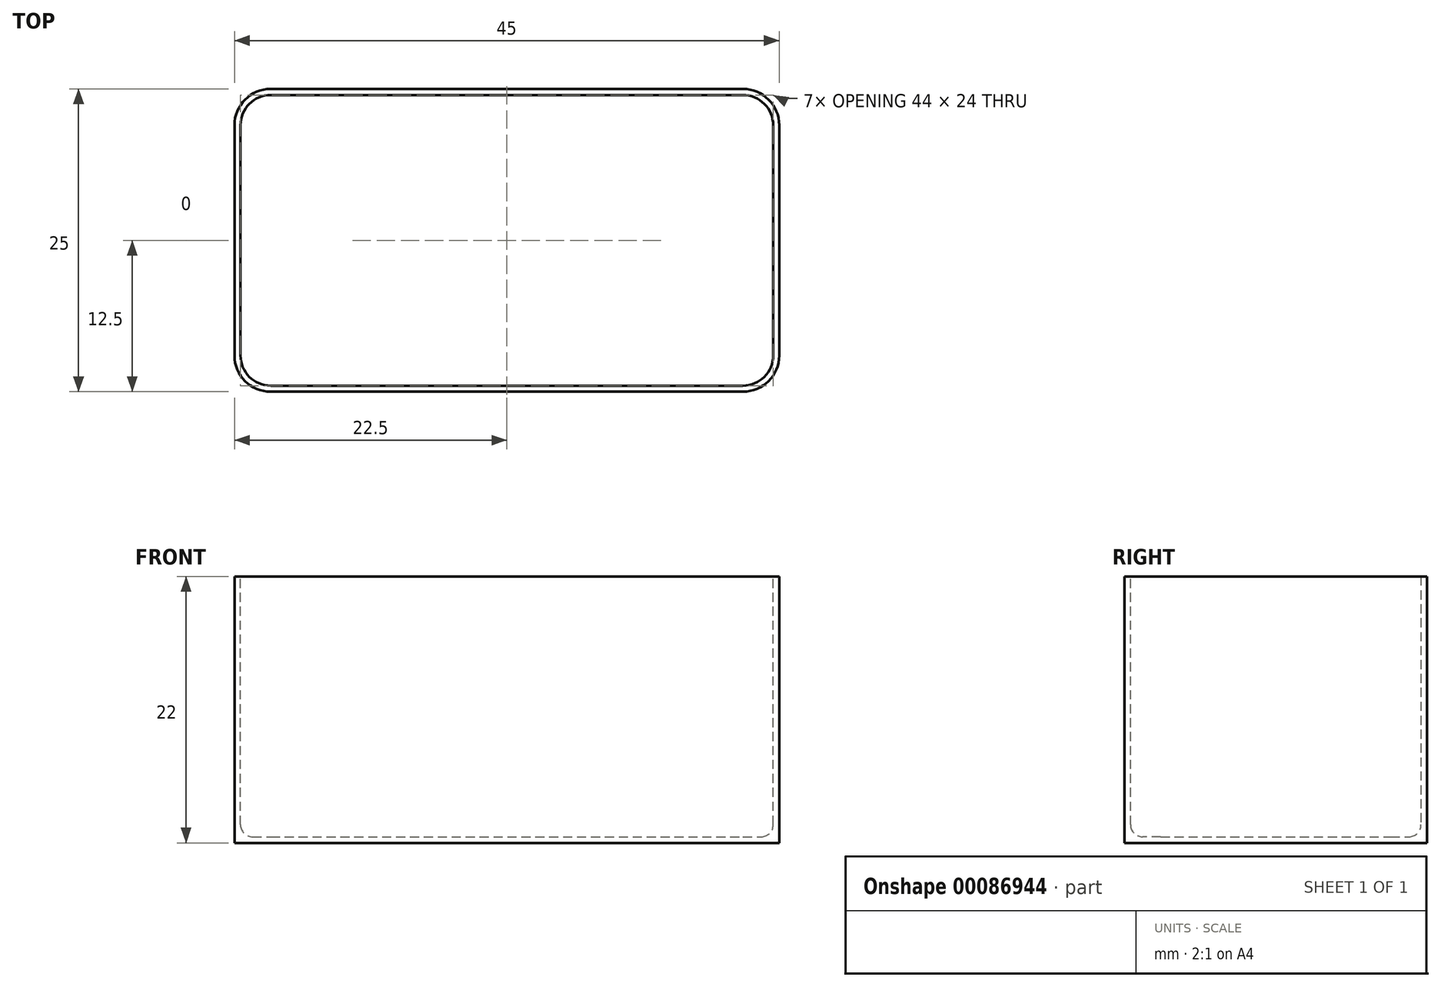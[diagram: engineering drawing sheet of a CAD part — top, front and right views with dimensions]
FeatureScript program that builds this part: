
annotation { "Feature Type Name" : "Feature", "Feature Type Description" : "" }
export const myFeature = defineFeature(function(context is Context, id is Id, definition is map)
    precondition{}
    {
        {
            var Q0;
            Q0=qCreatedBy(makeId("Top.planeOp"),FACE);
            var sketch = newSketch(context, id + "F0", { "sketchPlane" : qUnion([Q0])});
            skLineSegment(sketch, "E0.bottom", {"start": v(3, 0) * mm, "end": v(42, 0) * mm});
            skLineSegment(sketch, "E0.top", {"start": v(3, 25) * mm, "end": v(42, 25) * mm});
            skLineSegment(sketch, "E0.left", {"start": v(0, 3) * mm, "end": v(0, 22) * mm});
            skLineSegment(sketch, "E0.right", {"start": v(45, 3) * mm, "end": v(45, 22) * mm});
            skPoint(sketch, "E1.visualSharp", {"position": v(0, 25) * mm});
            skArc(sketch, "E1.filletArc", {"start": v(3, 25) * mm, "mid": v(0.88, 24.12) * mm, "end": v(0, 22) * mm});
            skPoint(sketch, "E2.visualSharp", {"position": v(45, 25) * mm});
            skArc(sketch, "E2.filletArc", {"start": v(45, 22) * mm, "mid": v(44.12, 24.12) * mm, "end": v(42, 25) * mm});
            skPoint(sketch, "E3.visualSharp", {"position": v(0, 0) * mm});
            skArc(sketch, "E3.filletArc", {"start": v(0, 3) * mm, "mid": v(0.88, 0.88) * mm, "end": v(3, 0) * mm});
            skPoint(sketch, "E4.visualSharp", {"position": v(45, 0) * mm});
            skArc(sketch, "E4.filletArc", {"start": v(42, 0) * mm, "mid": v(44.12, 0.88) * mm, "end": v(45, 3) * mm});
            skSolve(sketch);
        }
        {
            var Q0;
            Q0=makeQuery(id+"F0.imprint","IMPRINT",FACE,{"disambiguationData":[TD([[makeQuery(id+"F0.imprint","IMPRINT",EDGE,{"derivedFrom":sQuery(id+"F0.wireOp",EDGE,"E0.bottom")}),1.0]])]});
            extrude(context, id + "F1", {"entities" : qUnion([Q0]), "depth" : 22 * mm});
        }
        {
            var Q0;
            Q0=makeQuery(id+"F1.opExtrude","CAP_FACE",FACE,{"disambiguationData":[OSD([sQuery(id+"F0.wireOp",EDGE,"E0.bottom"),sQuery(id+"F0.wireOp",EDGE,"E0.top"),sQuery(id+"F0.wireOp",EDGE,"E0.left"),sQuery(id+"F0.wireOp",EDGE,"E0.right"),sQuery(id+"F0.wireOp",EDGE,"E1.filletArc"),sQuery(id+"F0.wireOp",EDGE,"E2.filletArc"),sQuery(id+"F0.wireOp",EDGE,"E3.filletArc"),sQuery(id+"F0.wireOp",EDGE,"E4.filletArc")])],"isStart":false});
            shell(context, id + "F2", {"entities" : qUnion([Q0]), "thickness" : 0.5 * mm});
        }
        {
            var Q0;
            Q0=makeQuery(id+"F2.opShell","OFFSET_FACE",FACE,{"disambiguationData":[OSD([sQuery(id+"F0.wireOp",EDGE,"E0.bottom"),sQuery(id+"F0.wireOp",EDGE,"E0.top"),sQuery(id+"F0.wireOp",EDGE,"E0.left"),sQuery(id+"F0.wireOp",EDGE,"E0.right"),sQuery(id+"F0.wireOp",EDGE,"E1.filletArc"),sQuery(id+"F0.wireOp",EDGE,"E2.filletArc"),sQuery(id+"F0.wireOp",EDGE,"E3.filletArc"),sQuery(id+"F0.wireOp",EDGE,"E4.filletArc")])]});
            fillet(context, id + "F3", {"entities" : qUnion([Q0]), "radius" : 1 * mm, "tangentPropagation" : true, "allowEdgeOverflow" : false});
        }
    });
